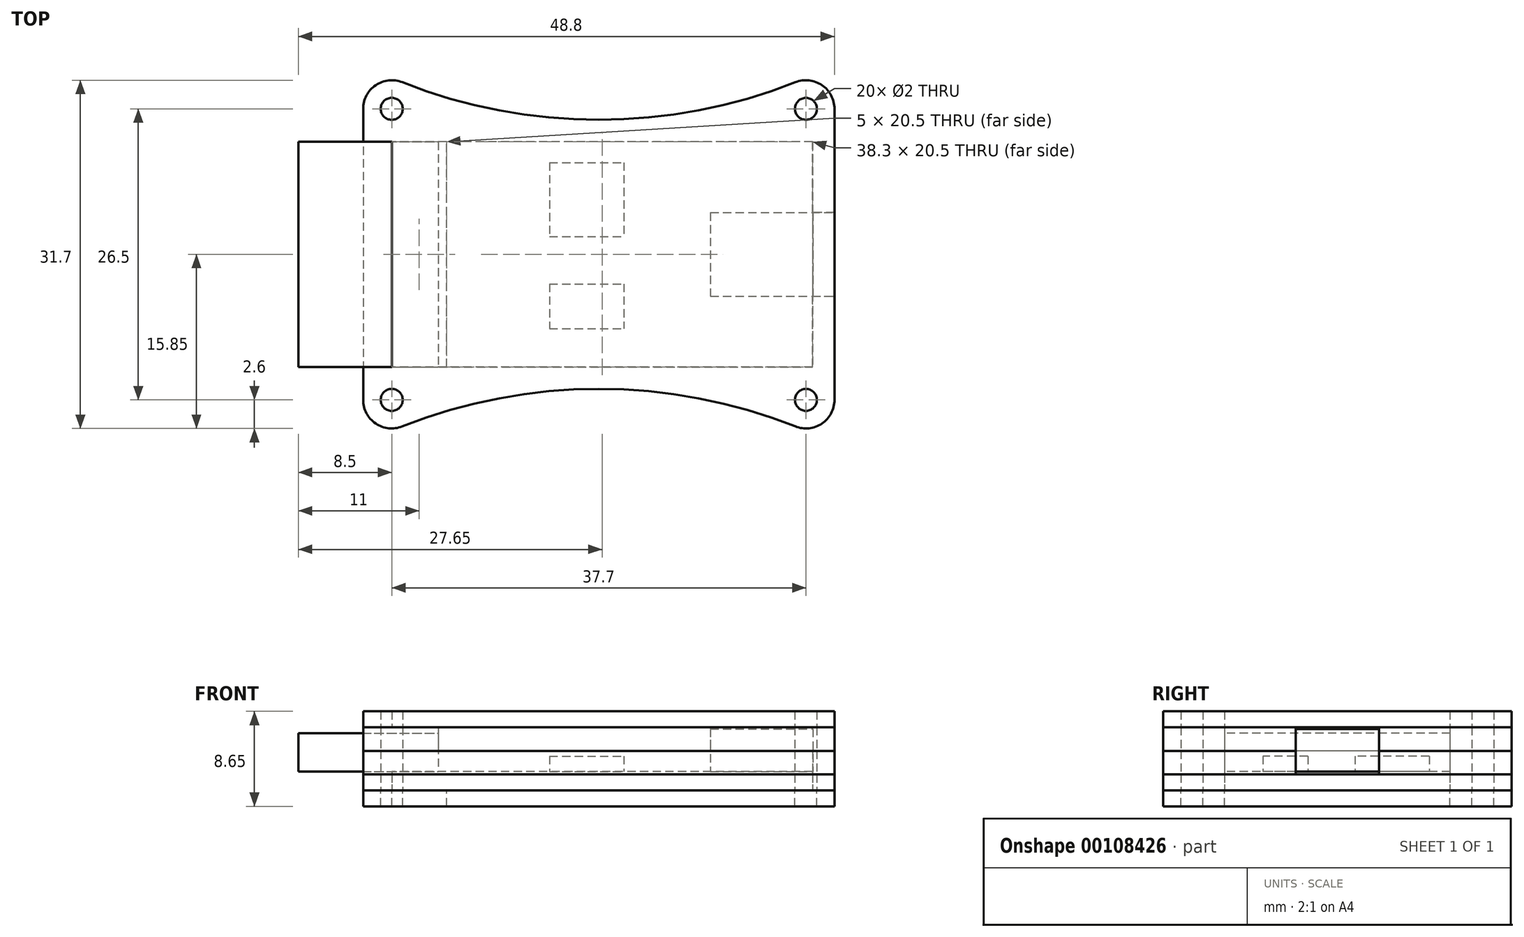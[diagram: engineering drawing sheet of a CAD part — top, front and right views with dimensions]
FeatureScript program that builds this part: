
annotation { "Feature Type Name" : "Feature", "Feature Type Description" : "" }
export const myFeature = defineFeature(function(context is Context, id is Id, definition is map)
    precondition{}
    {
        {
            var Q0;
            Q0=qCreatedBy(makeId("Top.planeOp"),FACE);
            var sketch = newSketch(context, id + "F0", { "sketchPlane" : qUnion([Q0])});
            skLineSegment(sketch, "E0.bottom", {"start": v(19.15, 10.25) * mm, "end": v(-19.15, 10.25) * mm});
            skLineSegment(sketch, "E0.top", {"start": v(19.15, -10.25) * mm, "end": v(-19.15, -10.25) * mm});
            skLineSegment(sketch, "E0.left", {"start": v(19.15, 10.25) * mm, "end": v(19.15, -10.25) * mm});
            skLineSegment(sketch, "E0.right", {"start": v(-19.15, 10.25) * mm, "end": v(-19.15, -10.25) * mm});
            skPoint(sketch, "E0.middle", {"position": v(0, 0) * mm});
            skSolve(sketch);
        }
        {
            var Q0;
            Q0=makeQuery(id+"F0.imprint","IMPRINT",FACE,{"disambiguationData":[TD([[makeQuery(id+"F0.imprint","IMPRINT",EDGE,{"derivedFrom":sQuery(id+"F0.wireOp",EDGE,"E0.bottom")}),1.0]])]});
            extrude(context, id + "F1", {"entities" : qUnion([Q0]), "depth" : 1.7 * mm});
        }
        {
            var Q0;
            Q0=makeQuery(id+"F1.opExtrude","CAP_FACE",FACE,{"disambiguationData":[OSD([sQuery(id+"F0.wireOp",EDGE,"E0.bottom"),sQuery(id+"F0.wireOp",EDGE,"E0.top"),sQuery(id+"F0.wireOp",EDGE,"E0.left"),sQuery(id+"F0.wireOp",EDGE,"E0.right")])],"isStart":false});
            var sketch = newSketch(context, id + "F2", { "sketchPlane" : qUnion([Q0])});
            skLineSegment(sketch, "E1.bottom", {"start": v(-4.79, 8.36) * mm, "end": v(1.96, 8.36) * mm});
            skLineSegment(sketch, "E1.top", {"start": v(-4.79, 1.61) * mm, "end": v(1.96, 1.61) * mm});
            skLineSegment(sketch, "E1.left", {"start": v(-4.79, 8.36) * mm, "end": v(-4.79, 1.61) * mm});
            skLineSegment(sketch, "E1.right", {"start": v(1.96, 8.36) * mm, "end": v(1.96, 1.61) * mm});
            skLineSegment(sketch, "E2.bottom", {"start": v(-4.79, -2.7) * mm, "end": v(1.96, -2.7) * mm});
            skLineSegment(sketch, "E2.top", {"start": v(-4.79, -6.76) * mm, "end": v(1.96, -6.76) * mm});
            skLineSegment(sketch, "E2.left", {"start": v(-4.79, -2.7) * mm, "end": v(-4.79, -6.76) * mm});
            skLineSegment(sketch, "E2.right", {"start": v(1.96, -2.7) * mm, "end": v(1.96, -6.76) * mm});
            skLineSegment(sketch, "E3.bottom", {"start": v(9.85, 3.8) * mm, "end": v(19.2, 3.8) * mm});
            skLineSegment(sketch, "E3.top", {"start": v(9.85, -3.8) * mm, "end": v(19.2, -3.8) * mm});
            skLineSegment(sketch, "E3.left", {"start": v(9.85, 3.8) * mm, "end": v(9.85, -3.8) * mm});
            skLineSegment(sketch, "E3.right", {"start": v(19.2, 3.8) * mm, "end": v(19.2, -3.8) * mm});
            skLineSegment(sketch, "E4", {"start": v(9.85, 0) * mm, "end": v(0, 0) * mm, "construction": true});
            skLineSegment(sketch, "E5.bottom", {"start": v(-27.65, 10.25) * mm, "end": v(-14.9, 10.25) * mm});
            skLineSegment(sketch, "E5.top", {"start": v(-27.65, -10.25) * mm, "end": v(-14.9, -10.25) * mm});
            skLineSegment(sketch, "E5.left", {"start": v(-27.65, 10.25) * mm, "end": v(-27.65, -10.25) * mm});
            skLineSegment(sketch, "E5.right", {"start": v(-14.9, 10.25) * mm, "end": v(-14.9, -10.25) * mm});
            skSolve(sketch);
        }
        {
            var Q0;
            {var subQ0=sQuery(id+"F2.wireOp",EDGE,"E3.left");Q0=makeQuery(id+"F2.imprint","IMPRINT",FACE,{"disambiguationData":[TD([[makeQuery(id+"F2.imprint","IMPRINT",EDGE,{"derivedFrom":subQ0}),1.0]])]});}
            var Q1;
            {var subQ0=sQuery(id+"F2.wireOp",EDGE,"E3.right");Q1=makeQuery(id+"F2.imprint","IMPRINT",FACE,{"disambiguationData":[TD([[makeQuery(id+"F2.imprint","IMPRINT",EDGE,{"derivedFrom":subQ0}),-1.0]])]});}
            extrude(context, id + "F3", {"entities" : qUnion([Q0, Q1]), "depth" : 3.9 * mm});
        }
        {
            var Q0;
            Q0=makeQuery(id+"F2.imprint","IMPRINT",FACE,{"disambiguationData":[TD([[makeQuery(id+"F2.imprint","IMPRINT",EDGE,{"derivedFrom":sQuery(id+"F2.wireOp",EDGE,"E1.bottom")}),-1.0]])]});
            var Q1;
            Q1=makeQuery(id+"F2.imprint","IMPRINT",FACE,{"disambiguationData":[TD([[makeQuery(id+"F2.imprint","IMPRINT",EDGE,{"derivedFrom":sQuery(id+"F2.wireOp",EDGE,"E2.bottom")}),-1.0]])]});
            extrude(context, id + "F4", {"entities" : qUnion([Q0, Q1]), "depth" : (3.12 - 1.7) * mm});
        }
        {
            var Q0;
            {var subQ2=sQuery(id+"F2.wireOp",EDGE,"E5.left");Q0=makeQuery(id+"F2.imprint","IMPRINT",FACE,{"disambiguationData":[TD([[makeQuery(id+"F2.imprint","IMPRINT",EDGE,{"derivedFrom":subQ2}),1.0]])]});}
            var Q1;
            {var subQ2=sQuery(id+"F2.wireOp",EDGE,"E5.right");Q1=makeQuery(id+"F2.imprint","IMPRINT",FACE,{"disambiguationData":[TD([[makeQuery(id+"F2.imprint","IMPRINT",EDGE,{"derivedFrom":subQ2}),-1.0]])]});}
            extrude(context, id + "F5", {"entities" : qUnion([Q0, Q1]), "depth" : (5.2 - 1.7) * mm});
        }
        {
            var Q0;
            Q0=qCreatedBy(makeId("Top.planeOp"),FACE);
            var sketch = newSketch(context, id + "F6", { "sketchPlane" : qUnion([Q0])});
            skLineSegment(sketch, "E6.left", {"start": v(-21.75, 13.25) * mm, "end": v(-21.75, -13.25) * mm});
            skLineSegment(sketch, "E6.right", {"start": v(21.15, 13.25) * mm, "end": v(21.15, -13.25) * mm});
            skLineSegment(sketch, "E7.0.0", {"start": v(19.15, -10.25) * mm, "end": v(19.15, 10.25) * mm});
            skLineSegment(sketch, "E7.0.1", {"start": v(19.15, 10.25) * mm, "end": v(-19.15, 10.25) * mm});
            skLineSegment(sketch, "E7.0.2", {"start": v(-19.15, 10.25) * mm, "end": v(-19.15, -10.25) * mm});
            skLineSegment(sketch, "E7.0.3", {"start": v(-19.15, -10.25) * mm, "end": v(19.15, -10.25) * mm});
            skCircle(sketch, "E8", {"center": v(-19.15, 13.25) * mm, "radius": 1 * mm});
            skCircle(sketch, "E9", {"center": v(18.55, 13.25) * mm, "radius": 1 * mm});
            skCircle(sketch, "E10", {"center": v(18.55, -13.25) * mm, "radius": 1 * mm});
            skCircle(sketch, "E11", {"center": v(-19.15, -13.25) * mm, "radius": 1 * mm});
            skArc(sketch, "E12", {"start": v(-18.2, 15.67) * mm, "mid": v(-20.61, 15.4) * mm, "end": v(-21.75, 13.25) * mm});
            skArc(sketch, "E13", {"start": v(-21.75, -13.25) * mm, "mid": v(-20.61, -15.4) * mm, "end": v(-18.2, -15.67) * mm});
            skArc(sketch, "E14", {"start": v(17.6, -15.67) * mm, "mid": v(20.01, -15.4) * mm, "end": v(21.15, -13.25) * mm});
            skArc(sketch, "E15", {"start": v(21.15, 13.25) * mm, "mid": v(20.01, 15.4) * mm, "end": v(17.6, 15.67) * mm});
            skArc(sketch, "E16", {"start": v(17.6, -15.67) * mm, "mid": v(-0.3, -12.25) * mm, "end": v(-18.2, -15.67) * mm});
            skArc(sketch, "E17", {"start": v(-18.2, 15.67) * mm, "mid": v(-0.3, 12.25) * mm, "end": v(17.6, 15.67) * mm});
            skSolve(sketch);
        }
        {
            var Q0;
            Q0=makeQuery(id+"F6.imprint","IMPRINT",FACE,{"disambiguationData":[TD([[makeQuery(id+"F6.imprint","IMPRINT",EDGE,{"derivedFrom":sQuery(id+"F6.wireOp",EDGE,"E6.left")}),1.0]])]});
            extrude(context, id + "F7", {"entities" : qUnion([Q0]), "depth" : 1.45 * mm});
        }
        {
            var Q0;
            Q0=makeQuery(id+"F7.opExtrude","CAP_FACE",FACE,{"disambiguationData":[OSD([sQuery(id+"F6.wireOp",EDGE,"E6.left"),sQuery(id+"F6.wireOp",EDGE,"E6.right"),sQuery(id+"F6.wireOp",EDGE,"E7.0.0"),sQuery(id+"F6.wireOp",EDGE,"E7.0.1"),sQuery(id+"F6.wireOp",EDGE,"E7.0.2"),sQuery(id+"F6.wireOp",EDGE,"E7.0.3"),sQuery(id+"F6.wireOp",EDGE,"E8"),sQuery(id+"F6.wireOp",EDGE,"E9"),sQuery(id+"F6.wireOp",EDGE,"E10"),sQuery(id+"F6.wireOp",EDGE,"E11"),sQuery(id+"F6.wireOp",EDGE,"E12"),sQuery(id+"F6.wireOp",EDGE,"E13"),sQuery(id+"F6.wireOp",EDGE,"E14"),sQuery(id+"F6.wireOp",EDGE,"E15"),sQuery(id+"F6.wireOp",EDGE,"E16"),sQuery(id+"F6.wireOp",EDGE,"E17")])],"isStart":false});
            var sketch = newSketch(context, id + "F8", { "sketchPlane" : qUnion([Q0])});
            skArc(sketch, "E18.1.0", {"start": v(-18.2, 15.67) * mm, "mid": v(-20.61, 15.4) * mm, "end": v(-21.75, 13.25) * mm});
            skLineSegment(sketch, "E18.1.1", {"start": v(-21.75, 13.25) * mm, "end": v(-21.75, 10.25) * mm});
            skArc(sketch, "E18.1.2", {"start": v(-21.75, -13.25) * mm, "mid": v(-20.61, -15.4) * mm, "end": v(-18.2, -15.67) * mm});
            skArc(sketch, "E18.1.3", {"start": v(-18.2, -15.67) * mm, "mid": v(-0.3, -12.25) * mm, "end": v(17.6, -15.67) * mm});
            skArc(sketch, "E18.1.4", {"start": v(17.6, -15.67) * mm, "mid": v(20.01, -15.4) * mm, "end": v(21.15, -13.25) * mm});
            skLineSegment(sketch, "E18.1.5", {"start": v(21.15, -13.25) * mm, "end": v(21.15, 13.25) * mm});
            skArc(sketch, "E18.1.6", {"start": v(21.15, 13.25) * mm, "mid": v(20.01, 15.4) * mm, "end": v(17.6, 15.67) * mm});
            skArc(sketch, "E18.1.7", {"start": v(17.6, 15.67) * mm, "mid": v(-0.3, 12.25) * mm, "end": v(-18.2, 15.67) * mm});
            skCircle(sketch, "E19.0", {"center": v(-19.15, -13.25) * mm, "radius": 1 * mm});
            skCircle(sketch, "E20.0", {"center": v(18.55, -13.25) * mm, "radius": 1 * mm});
            skCircle(sketch, "E21.0", {"center": v(18.55, 13.25) * mm, "radius": 1 * mm});
            skCircle(sketch, "E22.0", {"center": v(-19.15, 13.25) * mm, "radius": 1 * mm});
            skLineSegment(sketch, "E23.0", {"start": v(19.15, 10.25) * mm, "end": v(-21.75, 10.25) * mm});
            skLineSegment(sketch, "E24.0", {"start": v(19.15, -10.25) * mm, "end": v(19.15, 10.25) * mm});
            skLineSegment(sketch, "E25.0", {"start": v(-21.75, -10.25) * mm, "end": v(19.15, -10.25) * mm});
            skLineSegment(sketch, "E26.trimOffspring", {"start": v(-21.75, -10.25) * mm, "end": v(-21.75, -13.25) * mm});
            skPoint(sketch, "E27.orphan", {"position": v(-19.15, -10.25) * mm});
            skPoint(sketch, "E28.orphan", {"position": v(-19.15, 10.25) * mm});
            skLineSegment(sketch, "E29.0.0", {"start": v(21.15, 3.8) * mm, "end": v(9.85, 3.8) * mm});
            skLineSegment(sketch, "E29.0.2", {"start": v(9.85, -3.8) * mm, "end": v(21.15, -3.8) * mm});
            skPoint(sketch, "E30.orphan", {"position": v(19.2, -3.8) * mm});
            skPoint(sketch, "E31.orphan", {"position": v(19.2, 3.8) * mm});
            skSolve(sketch);
        }
        {
            var Q0;
            Q0=makeQuery(id+"F8.imprint","IMPRINT",FACE,{"disambiguationData":[TD([[makeQuery(id+"F8.imprint","IMPRINT",EDGE,{"derivedFrom":sQuery(id+"F8.wireOp",EDGE,"E18.1.2")}),1.0]])]});
            var Q1;
            Q1=makeQuery(id+"F8.imprint","IMPRINT",FACE,{"disambiguationData":[TD([[makeQuery(id+"F8.imprint","IMPRINT",EDGE,{"derivedFrom":sQuery(id+"F8.wireOp",EDGE,"E18.1.0")}),1.0]])]});
            extrude(context, id + "F9", {"entities" : qUnion([Q0, Q1]), "depth" : 2.15 * mm});
        }
        {
            var Q0;
            Q0=makeQuery(id+"F9.opExtrude","CAP_FACE",FACE,{"disambiguationData":[OSD([sQuery(id+"F8.wireOp",EDGE,"E18.1.2"),sQuery(id+"F8.wireOp",EDGE,"E18.1.3"),sQuery(id+"F8.wireOp",EDGE,"E18.1.4"),sQuery(id+"F8.wireOp",EDGE,"E18.1.5"),sQuery(id+"F8.wireOp",EDGE,"E19.0"),sQuery(id+"F8.wireOp",EDGE,"E20.0"),sQuery(id+"F8.wireOp",EDGE,"E24.0"),sQuery(id+"F8.wireOp",EDGE,"E25.0"),sQuery(id+"F8.wireOp",EDGE,"E26.trimOffspring"),sQuery(id+"F8.wireOp",EDGE,"E29.0.2")])],"isStart":false});
            var sketch = newSketch(context, id + "F10", { "sketchPlane" : qUnion([Q0])});
            skArc(sketch, "E32.0.0", {"start": v(-18.2, 15.67) * mm, "mid": v(-20.61, 15.4) * mm, "end": v(-21.75, 13.25) * mm});
            skLineSegment(sketch, "E32.0.1", {"start": v(-21.75, 13.25) * mm, "end": v(-21.75, 10.25) * mm});
            skArc(sketch, "E32.0.2", {"start": v(-21.75, -13.25) * mm, "mid": v(-20.61, -15.4) * mm, "end": v(-18.2, -15.67) * mm});
            skArc(sketch, "E32.0.3", {"start": v(-18.2, -15.67) * mm, "mid": v(-0.3, -12.25) * mm, "end": v(17.6, -15.67) * mm});
            skArc(sketch, "E32.0.4", {"start": v(17.6, -15.67) * mm, "mid": v(20.01, -15.4) * mm, "end": v(21.15, -13.25) * mm});
            skLineSegment(sketch, "E32.0.5", {"start": v(21.15, -13.25) * mm, "end": v(21.15, -3.8) * mm});
            skArc(sketch, "E32.0.6", {"start": v(21.15, 13.25) * mm, "mid": v(20.01, 15.4) * mm, "end": v(17.6, 15.67) * mm});
            skArc(sketch, "E32.0.7", {"start": v(17.6, 15.67) * mm, "mid": v(-0.3, 12.25) * mm, "end": v(-18.2, 15.67) * mm});
            skLineSegment(sketch, "E33.0", {"start": v(-14.9, 10.25) * mm, "end": v(-14.9, -10.25) * mm});
            skLineSegment(sketch, "E34", {"start": v(-14.9, 10.25) * mm, "end": v(-21.75, 10.25) * mm});
            skLineSegment(sketch, "E35", {"start": v(-14.9, -10.25) * mm, "end": v(-21.75, -10.25) * mm});
            skLineSegment(sketch, "E36.trimOffspring", {"start": v(-21.75, -10.25) * mm, "end": v(-21.75, -13.25) * mm});
            skLineSegment(sketch, "E37.0", {"start": v(9.85, 3.8) * mm, "end": v(21.15, 3.8) * mm});
            skLineSegment(sketch, "E37.1", {"start": v(9.85, 3.8) * mm, "end": v(9.85, -3.8) * mm});
            skLineSegment(sketch, "E37.2", {"start": v(9.85, -3.8) * mm, "end": v(21.15, -3.8) * mm});
            skPoint(sketch, "E38.orphan", {"position": v(19.2, 3.8) * mm});
            skPoint(sketch, "E39.orphan", {"position": v(19.2, -3.8) * mm});
            skLineSegment(sketch, "E40.trimOffspring", {"start": v(21.15, 3.8) * mm, "end": v(21.15, 13.25) * mm});
            skCircle(sketch, "E41.0", {"center": v(-19.15, -13.25) * mm, "radius": 1 * mm});
            skCircle(sketch, "E41.1", {"center": v(18.55, -13.25) * mm, "radius": 1 * mm});
            skCircle(sketch, "E41.2", {"center": v(18.55, 13.25) * mm, "radius": 1 * mm});
            skCircle(sketch, "E41.3", {"center": v(-19.15, 13.25) * mm, "radius": 1 * mm});
            skSolve(sketch);
        }
        {
            var Q0;
            Q0 = qSketchRegion(id + "F10", true);
            extrude(context, id + "F11", {"entities" : qUnion([Q0]), "depth" : 2.15 * mm});
        }
        {
            var Q0;
            Q0=makeQuery(id+"F7.opExtrude","CAP_FACE",FACE,{"disambiguationData":[OSD([sQuery(id+"F6.wireOp",EDGE,"E6.left"),sQuery(id+"F6.wireOp",EDGE,"E6.right"),sQuery(id+"F6.wireOp",EDGE,"E7.0.0"),sQuery(id+"F6.wireOp",EDGE,"E7.0.1"),sQuery(id+"F6.wireOp",EDGE,"E7.0.2"),sQuery(id+"F6.wireOp",EDGE,"E7.0.3"),sQuery(id+"F6.wireOp",EDGE,"E8"),sQuery(id+"F6.wireOp",EDGE,"E9"),sQuery(id+"F6.wireOp",EDGE,"E10"),sQuery(id+"F6.wireOp",EDGE,"E11"),sQuery(id+"F6.wireOp",EDGE,"E12"),sQuery(id+"F6.wireOp",EDGE,"E13"),sQuery(id+"F6.wireOp",EDGE,"E14"),sQuery(id+"F6.wireOp",EDGE,"E15"),sQuery(id+"F6.wireOp",EDGE,"E16"),sQuery(id+"F6.wireOp",EDGE,"E17")])],"isStart":true});
            var sketch = newSketch(context, id + "F12", { "sketchPlane" : qUnion([Q0])});
            skArc(sketch, "E42.0.0", {"start": v(-21.75, -13.25) * mm, "mid": v(-20.61, -15.4) * mm, "end": v(-18.2, -15.67) * mm});
            skArc(sketch, "E42.0.1", {"start": v(-18.2, -15.67) * mm, "mid": v(-0.3, -12.25) * mm, "end": v(17.6, -15.67) * mm});
            skArc(sketch, "E42.0.2", {"start": v(17.6, -15.67) * mm, "mid": v(20.01, -15.4) * mm, "end": v(21.15, -13.25) * mm});
            skLineSegment(sketch, "E42.0.3", {"start": v(21.15, -13.25) * mm, "end": v(21.15, 13.25) * mm});
            skArc(sketch, "E42.0.4", {"start": v(21.15, 13.25) * mm, "mid": v(20.01, 15.4) * mm, "end": v(17.6, 15.67) * mm});
            skArc(sketch, "E42.0.5", {"start": v(17.6, 15.67) * mm, "mid": v(-0.3, 12.25) * mm, "end": v(-18.2, 15.67) * mm});
            skArc(sketch, "E42.0.6", {"start": v(-18.2, 15.67) * mm, "mid": v(-20.61, 15.4) * mm, "end": v(-21.75, 13.25) * mm});
            skLineSegment(sketch, "E42.0.7", {"start": v(-21.75, 13.25) * mm, "end": v(-21.75, -13.25) * mm});
            skCircle(sketch, "E43.0", {"center": v(-19.15, 13.25) * mm, "radius": 1 * mm});
            skCircle(sketch, "E43.1", {"center": v(-19.15, -13.25) * mm, "radius": 1 * mm});
            skCircle(sketch, "E43.2", {"center": v(18.55, 13.25) * mm, "radius": 1 * mm});
            skCircle(sketch, "E43.3", {"center": v(18.55, -13.25) * mm, "radius": 1 * mm});
            skLineSegment(sketch, "E44", {"start": v(-14.15, 10.25) * mm, "end": v(-14.15, -10.25) * mm});
            skLineSegment(sketch, "E45.0", {"start": v(-19.15, -10.25) * mm, "end": v(-19.15, 10.25) * mm});
            skLineSegment(sketch, "E46", {"start": v(-14.15, 10.25) * mm, "end": v(-19.15, 10.25) * mm});
            skLineSegment(sketch, "E47", {"start": v(-14.15, -10.25) * mm, "end": v(-19.15, -10.25) * mm});
            skSolve(sketch);
        }
        {
            var Q0;
            Q0=makeQuery(id+"F12.imprint","IMPRINT",FACE,{"disambiguationData":[TD([[makeQuery(id+"F12.imprint","IMPRINT",EDGE,{"derivedFrom":sQuery(id+"F12.wireOp",EDGE,"E42.0.0")}),-1.0]])]});
            var Q1;
            {var subQ0=sQuery(id+"F12.wireOp",EDGE,"E44");Q1=makeQuery(id+"F12.imprint","IMPRINT",FACE,{"disambiguationData":[TD([[makeQuery(id+"F12.imprint","IMPRINT",EDGE,{"derivedFrom":subQ0}),1.0]])]});}
            extrude(context, id + "F13", {"entities" : qUnion([Q0, Q1]), "depth" : 1.45 * mm});
        }
        {
            var Q0;
            Q0=makeQuery(id+"F11.opExtrude","CAP_FACE",FACE,{"disambiguationData":[OSD([sQuery(id+"F10.wireOp",EDGE,"E32.0.0"),sQuery(id+"F10.wireOp",EDGE,"E32.0.1"),sQuery(id+"F10.wireOp",EDGE,"E32.0.2"),sQuery(id+"F10.wireOp",EDGE,"E32.0.3"),sQuery(id+"F10.wireOp",EDGE,"E32.0.4"),sQuery(id+"F10.wireOp",EDGE,"E32.0.5"),sQuery(id+"F10.wireOp",EDGE,"E32.0.6"),sQuery(id+"F10.wireOp",EDGE,"E32.0.7"),sQuery(id+"F10.wireOp",EDGE,"E33.0"),sQuery(id+"F10.wireOp",EDGE,"E34"),sQuery(id+"F10.wireOp",EDGE,"E35"),sQuery(id+"F10.wireOp",EDGE,"E36.trimOffspring"),sQuery(id+"F10.wireOp",EDGE,"E37.0"),sQuery(id+"F10.wireOp",EDGE,"E37.1"),sQuery(id+"F10.wireOp",EDGE,"E37.2"),sQuery(id+"F10.wireOp",EDGE,"E40.trimOffspring"),sQuery(id+"F10.wireOp",EDGE,"E41.0"),sQuery(id+"F10.wireOp",EDGE,"E41.1"),sQuery(id+"F10.wireOp",EDGE,"E41.2"),sQuery(id+"F10.wireOp",EDGE,"E41.3")])],"isStart":false});
            var sketch = newSketch(context, id + "F14", { "sketchPlane" : qUnion([Q0])});
            skArc(sketch, "E48.0.0", {"start": v(-21.75, 13.25) * mm, "mid": v(-20.61, 15.4) * mm, "end": v(-18.2, 15.67) * mm});
            skArc(sketch, "E48.0.1", {"start": v(-18.2, 15.67) * mm, "mid": v(-0.3, 12.25) * mm, "end": v(17.6, 15.67) * mm});
            skArc(sketch, "E48.0.2", {"start": v(17.6, 15.67) * mm, "mid": v(20.01, 15.4) * mm, "end": v(21.15, 13.25) * mm});
            skLineSegment(sketch, "E48.0.3", {"start": v(21.15, 13.25) * mm, "end": v(21.15, -13.25) * mm});
            skArc(sketch, "E48.0.4", {"start": v(21.15, -13.25) * mm, "mid": v(20.01, -15.4) * mm, "end": v(17.6, -15.67) * mm});
            skArc(sketch, "E48.0.5", {"start": v(17.6, -15.67) * mm, "mid": v(-0.3, -12.25) * mm, "end": v(-18.2, -15.67) * mm});
            skArc(sketch, "E48.0.6", {"start": v(-18.2, -15.67) * mm, "mid": v(-20.61, -15.4) * mm, "end": v(-21.75, -13.25) * mm});
            skLineSegment(sketch, "E48.0.7", {"start": v(-21.75, 10.25) * mm, "end": v(-21.75, 13.25) * mm});
            skCircle(sketch, "E49.0", {"center": v(-19.15, -13.25) * mm, "radius": 1 * mm});
            skCircle(sketch, "E49.1", {"center": v(18.55, -13.25) * mm, "radius": 1 * mm});
            skCircle(sketch, "E49.2", {"center": v(18.55, 13.25) * mm, "radius": 1 * mm});
            skCircle(sketch, "E49.3", {"center": v(-19.15, 13.25) * mm, "radius": 1 * mm});
            skLineSegment(sketch, "E50.0", {"start": v(-19.15, 10.25) * mm, "end": v(-19.15, -10.25) * mm});
            skLineSegment(sketch, "E51", {"start": v(-19.15, 10.25) * mm, "end": v(-21.75, 10.25) * mm});
            skLineSegment(sketch, "E52", {"start": v(-19.15, -10.25) * mm, "end": v(-21.75, -10.25) * mm});
            skLineSegment(sketch, "E53", {"start": v(-21.75, -10.25) * mm, "end": v(-21.75, -13.25) * mm});
            skSolve(sketch);
        }
        {
            var Q0;
            Q0 = qSketchRegion(id + "F14", true);
            extrude(context, id + "F15", {"entities" : qUnion([Q0]), "depth" : 1.45 * mm});
        }
    });
